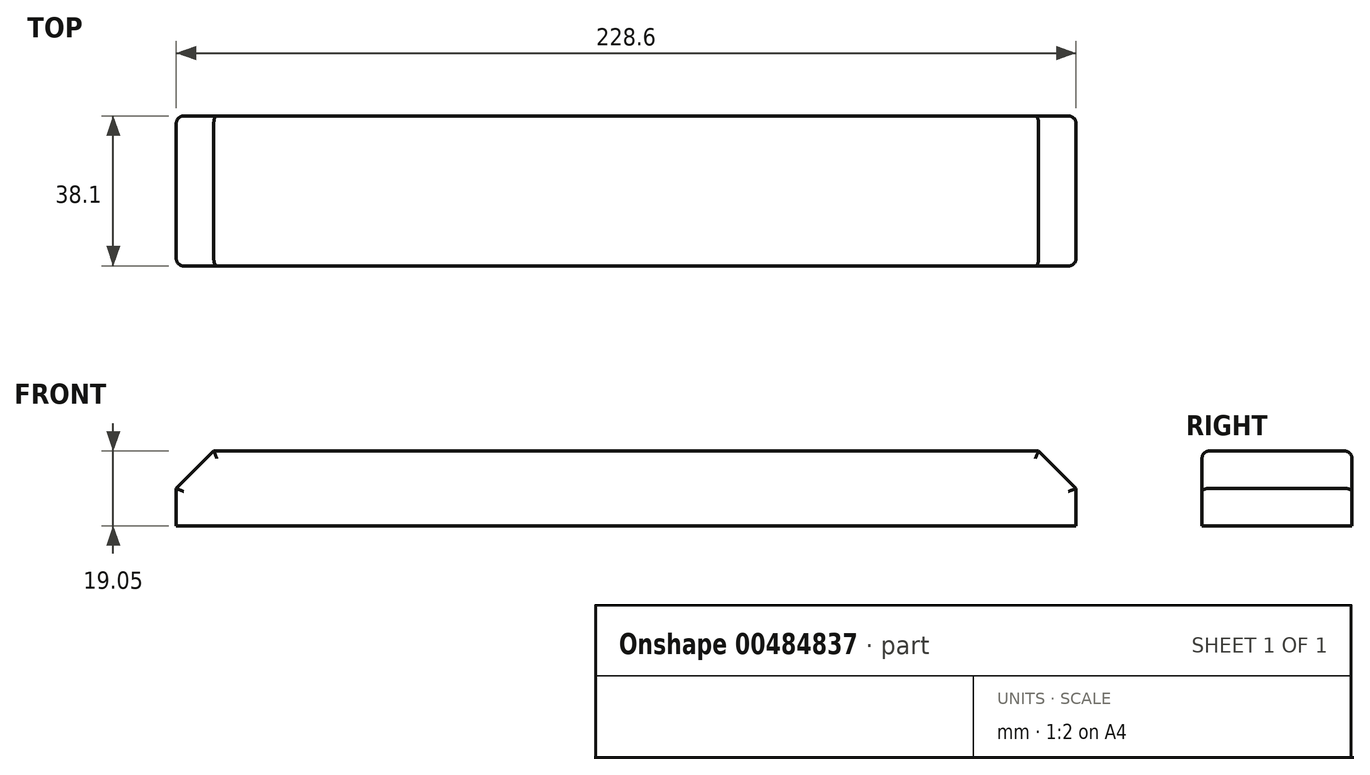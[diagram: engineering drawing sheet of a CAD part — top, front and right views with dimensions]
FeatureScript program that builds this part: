
annotation { "Feature Type Name" : "Feature", "Feature Type Description" : "" }
export const myFeature = defineFeature(function(context is Context, id is Id, definition is map)
    precondition{}
    {
        {
            var Q0;
            Q0=qCreatedBy(makeId("Right.planeOp"),FACE);
            var sketch = newSketch(context, id + "F0", { "sketchPlane" : qUnion([Q0])});
            skLineSegment(sketch, "E0.bottom", {"start": v(0, 0) * mm, "end": v(38.1, 0) * mm});
            skLineSegment(sketch, "E0.top", {"start": v(0, 19.05) * mm, "end": v(38.1, 19.05) * mm});
            skLineSegment(sketch, "E0.left", {"start": v(0, 0) * mm, "end": v(0, 19.05) * mm});
            skLineSegment(sketch, "E0.right", {"start": v(38.1, 0) * mm, "end": v(38.1, 19.05) * mm});
            skSolve(sketch);
        }
        {
            var Q0;
            Q0 = qSketchRegion(id + "F0", true);
            extrude(context, id + "F1", {"entities" : qUnion([Q0]), "depth" : 228.6 * mm});
        }
        {
            var Q0;
            Q0=makeQuery(id+"F1.opExtrude","CAP_EDGE",EDGE,{"disambiguationData":[OSD([sQuery(id+"F0.wireOp",EDGE,"E0.top")])],"isStart":true});
            var Q1;
            Q1=makeQuery(id+"F1.opExtrude","CAP_EDGE",EDGE,{"disambiguationData":[OSD([sQuery(id+"F0.wireOp",EDGE,"E0.top")])],"isStart":false});
            chamfer(context, id + "F2", {"entities" : qUnion([Q0, Q1]), "width" : 9.52 * mm, "tangentPropagation" : true});
        }
        {
            var Q0;
            Q0=makeQuery(id+"F1.opExtrude","SWEPT_EDGE",EDGE,{"disambiguationData":[OSD([sQuery(id+"F0.wireOp",EDGE,"E0.top"),sQuery(id+"F0.wireOp",EDGE,"E0.left")])]});
            var Q1;
            Q1=makeQuery(id+"F2.opChamfer","BLEND_EDGE",EDGE,{"blendedFrom":[makeQuery(id+"F1.opExtrude","CAP_EDGE",EDGE,{"disambiguationData":[OSD([sQuery(id+"F0.wireOp",EDGE,"E0.top")])],"isStart":true}),makeQuery(id+"F1.opExtrude","SWEPT_FACE",FACE,{"disambiguationData":[OSD([sQuery(id+"F0.wireOp",EDGE,"E0.left")])]})],"blendedInto":[makeQuery(id+"F1.opExtrude","SWEPT_FACE",FACE,{"disambiguationData":[OSD([sQuery(id+"F0.wireOp",EDGE,"E0.left")])]})]});
            var Q2;
            Q2=makeQuery(id+"F1.opExtrude","CAP_EDGE",EDGE,{"disambiguationData":[OSD([sQuery(id+"F0.wireOp",EDGE,"E0.left")])],"isStart":true});
            var Q3;
            Q3=makeQuery(id+"F2.opChamfer","BLEND_EDGE",EDGE,{"blendedFrom":[makeQuery(id+"F1.opExtrude","CAP_EDGE",EDGE,{"disambiguationData":[OSD([sQuery(id+"F0.wireOp",EDGE,"E0.top")])],"isStart":false}),makeQuery(id+"F1.opExtrude","SWEPT_FACE",FACE,{"disambiguationData":[OSD([sQuery(id+"F0.wireOp",EDGE,"E0.left")])]})],"blendedInto":[makeQuery(id+"F1.opExtrude","SWEPT_FACE",FACE,{"disambiguationData":[OSD([sQuery(id+"F0.wireOp",EDGE,"E0.left")])]})]});
            var Q4;
            Q4=makeQuery(id+"F1.opExtrude","CAP_EDGE",EDGE,{"disambiguationData":[OSD([sQuery(id+"F0.wireOp",EDGE,"E0.left")])],"isStart":false});
            var Q5;
            Q5=makeQuery(id+"F1.opExtrude","SWEPT_EDGE",EDGE,{"disambiguationData":[OSD([sQuery(id+"F0.wireOp",EDGE,"E0.top"),sQuery(id+"F0.wireOp",EDGE,"E0.right")])]});
            var Q6;
            Q6=makeQuery(id+"F2.opChamfer","BLEND_EDGE",EDGE,{"blendedFrom":[makeQuery(id+"F1.opExtrude","CAP_EDGE",EDGE,{"disambiguationData":[OSD([sQuery(id+"F0.wireOp",EDGE,"E0.top")])],"isStart":true}),makeQuery(id+"F1.opExtrude","SWEPT_FACE",FACE,{"disambiguationData":[OSD([sQuery(id+"F0.wireOp",EDGE,"E0.right")])]})],"blendedInto":[makeQuery(id+"F1.opExtrude","SWEPT_FACE",FACE,{"disambiguationData":[OSD([sQuery(id+"F0.wireOp",EDGE,"E0.right")])]})]});
            var Q7;
            Q7=makeQuery(id+"F1.opExtrude","CAP_EDGE",EDGE,{"disambiguationData":[OSD([sQuery(id+"F0.wireOp",EDGE,"E0.right")])],"isStart":true});
            var Q8;
            Q8=makeQuery(id+"F2.opChamfer","BLEND_EDGE",EDGE,{"blendedFrom":[makeQuery(id+"F1.opExtrude","CAP_EDGE",EDGE,{"disambiguationData":[OSD([sQuery(id+"F0.wireOp",EDGE,"E0.top")])],"isStart":false}),makeQuery(id+"F1.opExtrude","SWEPT_FACE",FACE,{"disambiguationData":[OSD([sQuery(id+"F0.wireOp",EDGE,"E0.right")])]})],"blendedInto":[makeQuery(id+"F1.opExtrude","SWEPT_FACE",FACE,{"disambiguationData":[OSD([sQuery(id+"F0.wireOp",EDGE,"E0.right")])]})]});
            var Q9;
            Q9=makeQuery(id+"F1.opExtrude","CAP_EDGE",EDGE,{"disambiguationData":[OSD([sQuery(id+"F0.wireOp",EDGE,"E0.right")])],"isStart":false});
            fillet(context, id + "F3", {"entities" : qUnion([Q0, Q1, Q2, Q3, Q4, Q5, Q6, Q7, Q8, Q9]), "radius" : 1.9 * mm, "tangentPropagation" : true, "allowEdgeOverflow" : false});
        }
    });
